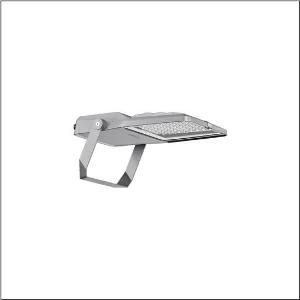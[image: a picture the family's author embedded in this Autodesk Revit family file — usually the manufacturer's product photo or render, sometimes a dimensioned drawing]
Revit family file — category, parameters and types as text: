
# Revit family: floodlight_fl_21_mini___pl43_5xa7775c2a1a_0644
name_source: partatom
category: Lighting Fixtures
units: mm (PartAtom-declared; Revit-internal decimal feet)

## family parameters
Cut with Voids When Loaded = No
Host = Face
Light Source = No
Part Type = Normal
Room Calculation Point = No
Round Connector Dimension = Use Diameter
Shared = No

## types (1)
- --- (1 x LED, 12500 lm, 89 W, 3000K)
    Apparent Load = 89 VA
    CIE Flux Codes = 27 78 99 100 100
    Color Rendering = 70
    Color Temperature = 3000K
    Default Elevation = 1800 mm
    Description = Floodlight FL 21 mini, floodlight, primary light control with lens, of PMMA, primary optical cover: protective disc, of toughened safety glass, transparent, light distribution: PL43, light emission: direct distribution, installation type: surface-mounted, LED, High Power LED, rated luminous flux: 12.500lm, luminous efficacy: 140lm/W, light colour: 730, colour temperature: 3000K, control: flexible luminous flux parameterisation, time-dependent luminous flux control, constant luminous flux control, overheat protection, presetting dimming logarithmic, with terminal, 6-pole, mains connection: 220..240V, AC, 50/60Hz, start of lifetime: 89W, end of service life: 94W, reduction: 43W, luminaire housing, of diecast aluminium, powder-coated, Siteco® metallic grey (DB 702S), corrosivity category C5 mid according to DIN EN ISO 12944, sealing non-destructively replaceable, mounting bracket, of steel, galvanised, powder-coated, Siteco® metallic grey (DB 702S), Smart Interface above, protection rating (complete): IP66, insulation class (complete): insulation class II (safety insulation), certification: CE, ENEC, VDE, protection symbol: D, impact resistance: IK08, permissible operating ambient temperature: -40..+40°C, permissible operating ambient temperature for outdoor applications: -40..+50°C, standard: DIN EN 12944, LABS conformity tested according to VDMA 24364:2018-05, packaging unit: 1 piece

Light Distribution: PL43
    Height = 70 mm
    Lamp = 1 x LED
    Lamp Light Flux = 12500 lm
    Lamp Power = 89 W
    Lamp count = 1
    Length = 485 mm
    Luminous efficacy = 140 lm/W
    Manufacturer = Siteco
    ModVariant = No
    Model = 5XA7775C2A1A
    Number of Poles = 1
    OnlyDefault = Yes
    Power Factor = 1
    Product Name = Floodlight FL 21 mini | PL43
    Product group = floodlight | pylon annexe
    ProductGroupID = 6200
    Protection Class = Protection class II
    Protection Degree = IP 66
    RLX_Detail_Level = 1
    RLX_Emergency_Light_Flux = 0 lm
    RLX_Emergency_Type = 0
    RLX_Emergency_Type_DB = No
    RlxData = <blob elided: 95673 chars, md5=f5d0db18>
    Socket = socket
    Standby Power = 0 W
    System Light Flux = 12500 lm
    System Power = 89 W
    Type Comments = factory setting: luminous flux: 100 % | dim-lin: 254 | 456 mA
    Type Image = l_1006845.jpg
    URL = http://relux.com
    VarID = @adj_111343
    Voltage = 0 V
    Weight = 0.00 kg
    Width = 337 mm

## geometry (parser evidence)
native form markers: Blend x4, Sweep x15
no freeform markers — native parametric forms only
